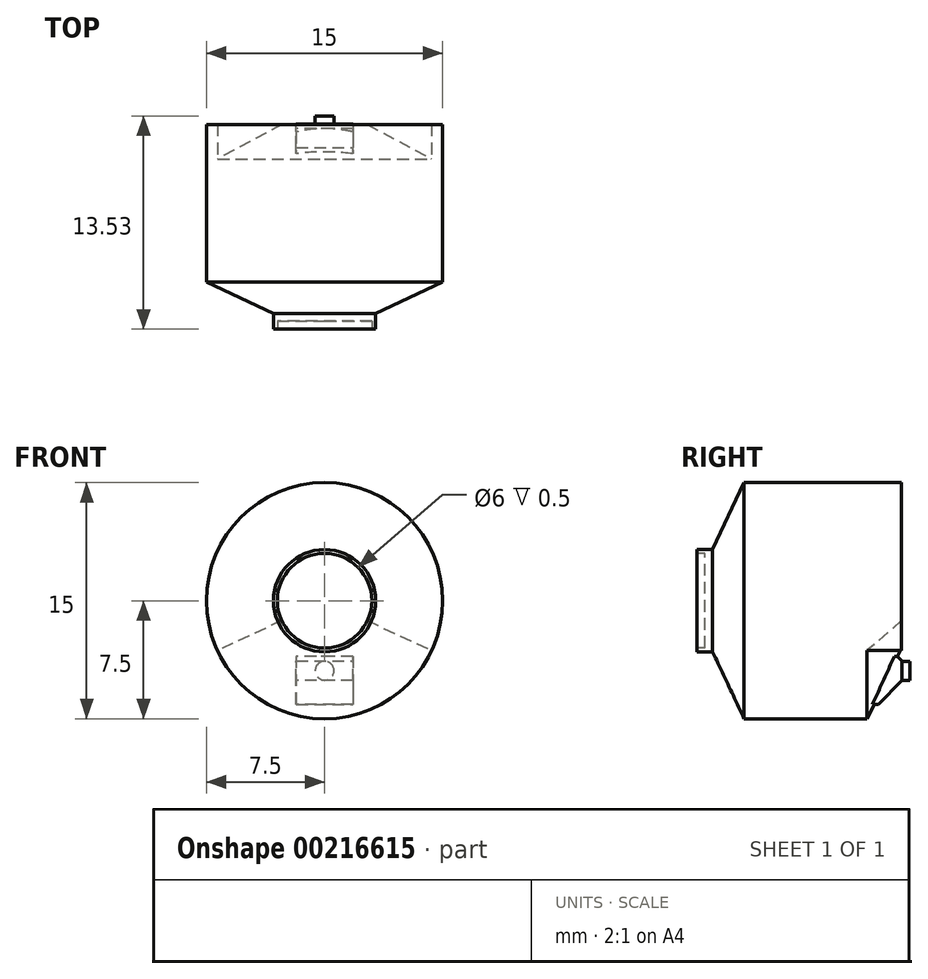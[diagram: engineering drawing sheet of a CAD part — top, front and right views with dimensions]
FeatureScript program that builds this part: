
annotation { "Feature Type Name" : "Feature", "Feature Type Description" : "" }
export const myFeature = defineFeature(function(context is Context, id is Id, definition is map)
    precondition{}
    {
        {
            var Q0;
            Q0=qCreatedBy(makeId("Front.planeOp"),FACE);
            var sketch = newSketch(context, id + "F0", { "sketchPlane" : qUnion([Q0])});
            skCircle(sketch, "E0", {"center": v(0, 0) * mm, "radius": 3.25 * mm});
            skSolve(sketch);
        }
        {
            var Q0;
            Q0=qCreatedBy(makeId("Front.planeOp"),FACE);
            cPlane(context, id + "F1", {"entities" : qUnion([Q0]), "cplaneType" : CPlaneType.OFFSET, "offset" : 2 * mm, "oppositeDirection" : true, "width" : 150 * mm, "height" : 150 * mm});
        }
        {
            var Q0;
            Q0=qCreatedBy(id+"F1.planeOp",FACE);
            var sketch = newSketch(context, id + "F2", { "sketchPlane" : qUnion([Q0])});
            skCircle(sketch, "E1", {"center": v(0, 0) * mm, "radius": 7.5 * mm});
            skSolve(sketch);
        }
        {
            var Q0;
            Q0=makeQuery(id+"F0.imprint","IMPRINT",FACE,{"disambiguationData":[TD([[makeQuery(id+"F0.imprint","IMPRINT",EDGE,{"derivedFrom":sQuery(id+"F0.wireOp",EDGE,"E0")}),1.0]])]});
            var Q1;
            Q1=makeQuery(id+"F2.imprint","IMPRINT",FACE,{"disambiguationData":[TD([[makeQuery(id+"F2.imprint","IMPRINT",EDGE,{"derivedFrom":sQuery(id+"F2.wireOp",EDGE,"E1")}),1.0]])]});
            loft(context, id + "F3", {"sheetProfilesArray" : [{ "sheetProfileEntities" : qUnion([Q0]) }, { "sheetProfileEntities" : qUnion([Q1]) }]});
        }
        {
            var Q0;
            Q0=makeQuery(id+"F3.opLoft","CAP_FACE",FACE,{"disambiguationData":[OSD([makeQuery(id+"F0.imprint","IMPRINT",FACE,{"disambiguationData":[TD([[makeQuery(id+"F0.imprint","IMPRINT",EDGE,{"derivedFrom":sQuery(id+"F0.wireOp",EDGE,"E0")}),1.0]])]})])],"isStart":true});
            extrude(context, id + "F4", {"entities" : qUnion([Q0]), "operationType" : NewBodyOperationType.ADD, "depth" : 1 * mm});
        }
        {
            var Q0;
            Q0=makeQuery(id+"F4.opExtrude","CAP_FACE",FACE,{"disambiguationData":[OSD([makeQuery(id+"F0.imprint","IMPRINT",FACE,{"disambiguationData":[TD([[makeQuery(id+"F0.imprint","IMPRINT",EDGE,{"derivedFrom":sQuery(id+"F0.wireOp",EDGE,"E0")}),1.0]])]})])],"isStart":false});
            var sketch = newSketch(context, id + "F5", { "sketchPlane" : qUnion([Q0])});
            skCircle(sketch, "E2", {"center": v(0, 0) * mm, "radius": 3 * mm});
            skSolve(sketch);
        }
        {
            var Q0;
            Q0=makeQuery(id+"F5.imprint","IMPRINT",FACE,{"disambiguationData":[TD([[makeQuery(id+"F5.imprint","IMPRINT",EDGE,{"derivedFrom":sQuery(id+"F5.wireOp",EDGE,"E2")}),1.0]])]});
            extrude(context, id + "F6", {"entities" : qUnion([Q0]), "operationType" : NewBodyOperationType.REMOVE, "oppositeDirection" : true, "depth" : .5 * mm});
        }
        {
            var Q0;
            Q0=makeQuery(id+"F3.opLoft","CAP_FACE",FACE,{"disambiguationData":[OSD([makeQuery(id+"F2.imprint","IMPRINT",FACE,{"disambiguationData":[TD([[makeQuery(id+"F2.imprint","IMPRINT",EDGE,{"derivedFrom":sQuery(id+"F2.wireOp",EDGE,"E1")}),1.0]])]})])],"isStart":true});
            extrude(context, id + "F7", {"entities" : qUnion([Q0]), "operationType" : NewBodyOperationType.ADD, "depth" : 10 * mm});
        }
        {
            var Q0;
            Q0=qCreatedBy(makeId("Right.planeOp"),FACE);
            var sketch = newSketch(context, id + "F8", { "sketchPlane" : qUnion([Q0])});
            skLineSegment(sketch, "E3", {"start": v(0, 0) * mm, "end": v(12, 0) * mm});
            skLineSegment(sketch, "E4", {"start": v(12, 0) * mm, "end": v(12, -3) * mm});
            skLineSegment(sketch, "E5", {"start": v(6.79, -8.67) * mm, "end": v(13.18, -8.67) * mm});
            skLineSegment(sketch, "E6", {"start": v(13.18, -8.67) * mm, "end": v(13.18, -3) * mm});
            skLineSegment(sketch, "E7", {"start": v(13.18, -3) * mm, "end": v(12, -3) * mm});
            skLineSegment(sketch, "E8", {"start": v(12, -3) * mm, "end": v(9.24, -8.67) * mm});
            skSolve(sketch);
        }
        {
            var Q0;
            {var subQ0=sQuery(id+"F8.wireOp",EDGE,"E6");Q0=makeQuery(id+"F8.imprint","IMPRINT",FACE,{"disambiguationData":[TD([[makeQuery(id+"F8.imprint","IMPRINT",EDGE,{"derivedFrom":subQ0}),1.0]])]});}
            var Q1;
            Q1=sQuery(id+"F8.wireOp",EDGE,"E3");
            revolve(context, id + "F9", {"operationType" : NewBodyOperationType.REMOVE, "entities" : qUnion([Q0]), "axis" : qUnion([Q1]), "revolveType" : RevolveType.SYMMETRIC, "oppositeDirection" : true, "angle" : 130 * degree});
        }
        {
            var Q0;
            Q0=qCreatedBy(makeId("Right.planeOp"),FACE);
            var sketch = newSketch(context, id + "F10", { "sketchPlane" : qUnion([Q0])});
            skLineSegment(sketch, "E9.bottom", {"start": v(9.98, -6.57) * mm, "end": v(12.03, -6.57) * mm});
            skLineSegment(sketch, "E9.left", {"start": v(9.98, -6.57) * mm, "end": v(9.98, -3.89) * mm});
            skLineSegment(sketch, "E9.right", {"start": v(12.03, -6.57) * mm, "end": v(12.03, -3.89) * mm});
            skLineSegment(sketch, "E10.top", {"start": v(9.98, -3.52) * mm, "end": v(12.03, -3.52) * mm});
            skLineSegment(sketch, "E10.left", {"start": v(9.98, -3.89) * mm, "end": v(9.98, -3.52) * mm});
            skLineSegment(sketch, "E10.right", {"start": v(12.03, -3.89) * mm, "end": v(12.03, -3.52) * mm});
            skSolve(sketch);
        }
        {
            var Q0;
            Q0=makeQuery(id+"F10.imprint","IMPRINT",FACE,{"disambiguationData":[TD([[makeQuery(id+"F10.imprint","IMPRINT",EDGE,{"derivedFrom":sQuery(id+"F10.wireOp",EDGE,"E9.bottom")}),1.0]])]});
            extrude(context, id + "F11", {"entities" : qUnion([Q0]), "operationType" : NewBodyOperationType.ADD, "oppositeDirection" : true, "depth" : 1.8 * mm, "hasSecondDirection" : true, "secondDirectionOppositeDirection" : false, "secondDirectionDepth" : 1.8 * mm});
        }
        {
            var Q0;
            Q0=makeQuery(id+"F11.opExtrude","SWEPT_EDGE",EDGE,{"disambiguationData":[OSD([sQuery(id+"F10.wireOp",EDGE,"E9.top"),sQuery(id+"F10.wireOp",EDGE,"E9.right")])]});
            chamfer(context, id + "F12", {"entities" : qUnion([Q0]), "width" : 1.5 * mm, "tangentPropagation" : true});
        }
        {
            var Q0;
            Q0=makeQuery(id+"F11.opExtrude","SWEPT_EDGE",EDGE,{"disambiguationData":[OSD([sQuery(id+"F10.wireOp",EDGE,"E10.top"),sQuery(id+"F10.wireOp",EDGE,"E10.right")])]});
            chamfer(context, id + "F13", {"entities" : qUnion([Q0]), "width" : .3 * mm, "tangentPropagation" : true});
        }
        {
            var Q0;
            Q0=makeQuery(id+"F11.opExtrude","SWEPT_FACE",FACE,{"disambiguationData":[OSD([sQuery(id+"F10.wireOp",EDGE,"E9.right"),sQuery(id+"F10.wireOp",EDGE,"E10.right")])]});
            var sketch = newSketch(context, id + "F14", { "sketchPlane" : qUnion([Q0])});
            skCircle(sketch, "E11", {"center": v(0, -4.45) * mm, "radius": 0.6 * mm});
            skPoint(sketch, "E11.centerSnap0", {"position": v(-1.8, -4.45) * mm});
            skSolve(sketch);
        }
        {
            var Q0;
            Q0=makeQuery(id+"F14.imprint","IMPRINT",FACE,{"disambiguationData":[TD([[makeQuery(id+"F14.imprint","IMPRINT",EDGE,{"derivedFrom":sQuery(id+"F14.wireOp",EDGE,"E11")}),1.0]])]});
            extrude(context, id + "F15", {"entities" : qUnion([Q0]), "operationType" : NewBodyOperationType.ADD, "depth" : .5 * mm});
        }
    });
